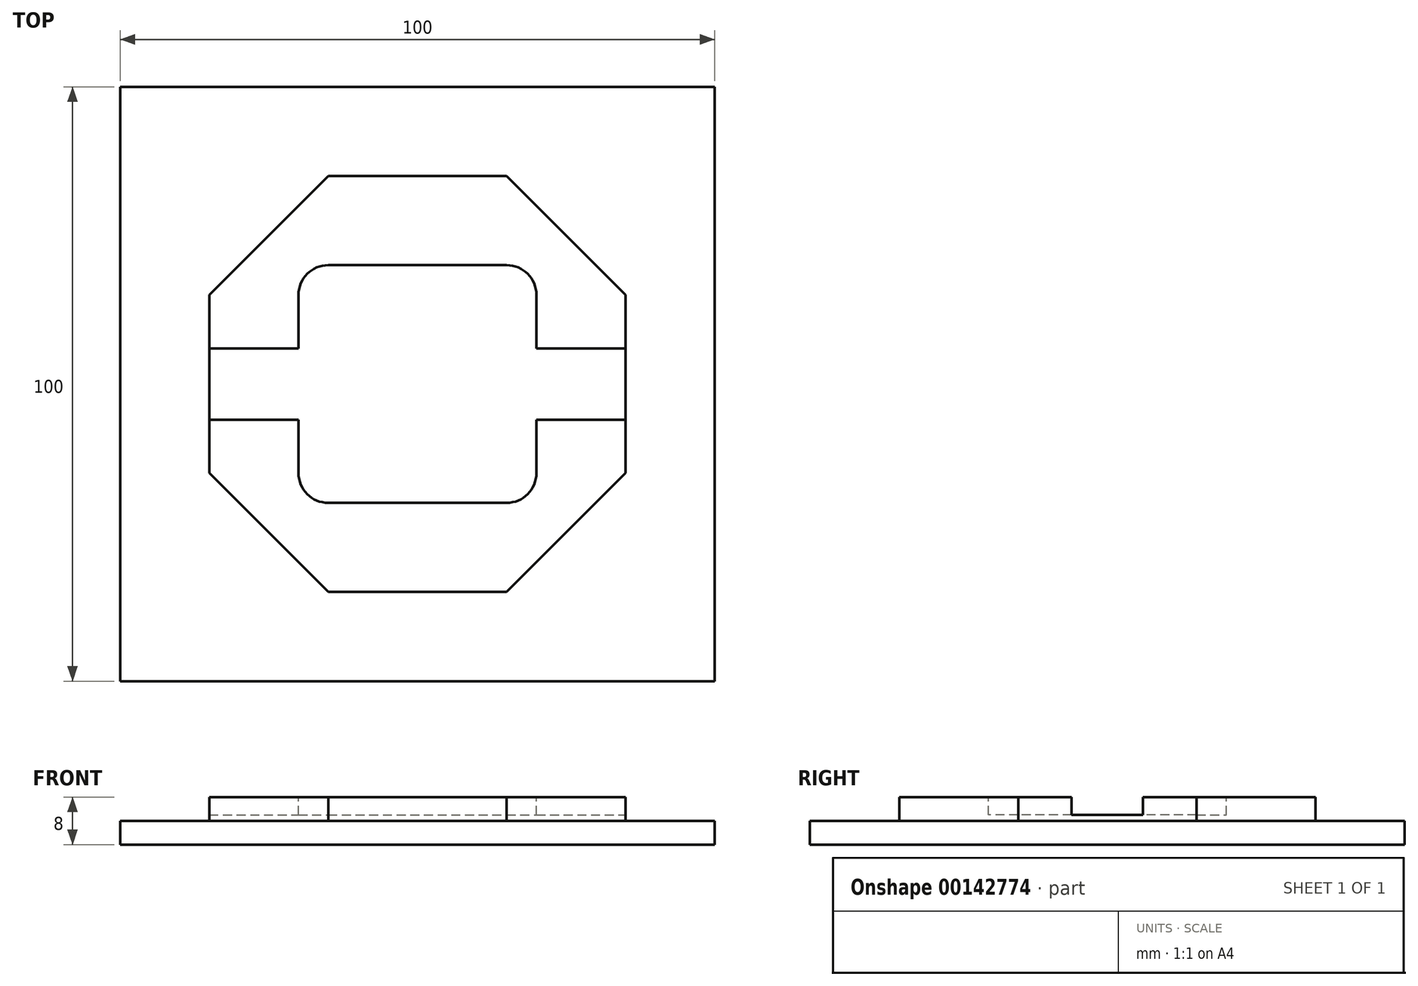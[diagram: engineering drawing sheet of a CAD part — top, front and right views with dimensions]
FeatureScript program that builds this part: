
annotation { "Feature Type Name" : "Feature", "Feature Type Description" : "" }
export const myFeature = defineFeature(function(context is Context, id is Id, definition is map)
    precondition{}
    {
        {
            var Q0;
            Q0=qCreatedBy(makeId("Top.planeOp"),FACE);
            var sketch = newSketch(context, id + "F0", { "sketchPlane" : qUnion([Q0])});
            skLineSegment(sketch, "E0.bottom", {"start": v(-50, -50) * mm, "end": v(50, -50) * mm});
            skLineSegment(sketch, "E0.top", {"start": v(-50, 50) * mm, "end": v(50, 50) * mm});
            skLineSegment(sketch, "E0.left", {"start": v(-50, -50) * mm, "end": v(-50, 50) * mm});
            skLineSegment(sketch, "E0.right", {"start": v(50, -50) * mm, "end": v(50, 50) * mm});
            skLineSegment(sketch, "E1", {"start": v(-50, 50) * mm, "end": v(50, -50) * mm, "construction": true});
            skSolve(sketch);
        }
        {
            var Q0;
            Q0=makeQuery(id+"F0.imprint","IMPRINT",FACE,{"disambiguationData":[TD([[makeQuery(id+"F0.imprint","IMPRINT",EDGE,{"derivedFrom":sQuery(id+"F0.wireOp",EDGE,"E0.bottom")}),1.0]])]});
            extrude(context, id + "F1", {"entities" : qUnion([Q0]), "depth" : 4 * mm});
        }
        {
            var Q0;
            Q0=makeQuery(id+"F1.opExtrude","CAP_FACE",FACE,{"disambiguationData":[OSD([sQuery(id+"F0.wireOp",EDGE,"E0.bottom"),sQuery(id+"F0.wireOp",EDGE,"E0.top"),sQuery(id+"F0.wireOp",EDGE,"E0.left"),sQuery(id+"F0.wireOp",EDGE,"E0.right")])],"isStart":false});
            var sketch = newSketch(context, id + "F2", { "sketchPlane" : qUnion([Q0])});
            skPoint(sketch, "E2.0", {"position": v(0, 0) * mm});
            skLineSegment(sketch, "E3.0", {"start": v(35, 15) * mm, "end": v(35, -15) * mm});
            skLineSegment(sketch, "E3.1", {"start": v(35, -15) * mm, "end": v(15, -35) * mm});
            skLineSegment(sketch, "E3.2", {"start": v(15, -35) * mm, "end": v(0, -35) * mm});
            skLineSegment(sketch, "E3.6", {"start": v(0, 35) * mm, "end": v(15, 35) * mm});
            skLineSegment(sketch, "E3.7", {"start": v(15, 35) * mm, "end": v(35, 15) * mm});
            skPoint(sketch, "E3.0.midPoint", {"position": v(35, 0) * mm});
            skLineSegment(sketch, "E4", {"start": v(0, -35) * mm, "end": v(0, 35) * mm, "construction": true});
            skLineSegment(sketch, "E5.MirrorCS", {"start": v(0, 35) * mm, "end": v(-15, 35) * mm});
            skLineSegment(sketch, "E6.MirrorCS", {"start": v(-15, 35) * mm, "end": v(-35, 15) * mm});
            skLineSegment(sketch, "E7.MirrorCS", {"start": v(-35, 15) * mm, "end": v(-35, -15) * mm});
            skLineSegment(sketch, "E8.MirrorCS", {"start": v(-35, -15) * mm, "end": v(-15, -35) * mm});
            skLineSegment(sketch, "E9.MirrorCS", {"start": v(-15, -35) * mm, "end": v(0, -35) * mm});
            skSolve(sketch);
        }
        {
            var Q0;
            Q0 = qSketchRegion(id + "F2", true);
            extrude(context, id + "F3", {"entities" : qUnion([Q0]), "operationType" : NewBodyOperationType.ADD, "depth" : 4 * mm});
        }
        {
            var Q0;
            Q0=makeQuery(id+"F3.opExtrude","CAP_FACE",FACE,{"disambiguationData":[OSD([sQuery(id+"F2.wireOp",EDGE,"E3.0"),sQuery(id+"F2.wireOp",EDGE,"E3.1"),sQuery(id+"F2.wireOp",EDGE,"E3.2"),sQuery(id+"F2.wireOp",EDGE,"E3.6"),sQuery(id+"F2.wireOp",EDGE,"E3.7"),sQuery(id+"F2.wireOp",EDGE,"E5.MirrorCS"),sQuery(id+"F2.wireOp",EDGE,"E6.MirrorCS"),sQuery(id+"F2.wireOp",EDGE,"E7.MirrorCS"),sQuery(id+"F2.wireOp",EDGE,"E8.MirrorCS"),sQuery(id+"F2.wireOp",EDGE,"E9.MirrorCS")])],"isStart":false});
            var sketch = newSketch(context, id + "F4", { "sketchPlane" : qUnion([Q0])});
            skLineSegment(sketch, "E10.bottom", {"start": v(-15, 20) * mm, "end": v(15, 20) * mm});
            skLineSegment(sketch, "E10.top", {"start": v(-15, -20) * mm, "end": v(15, -20) * mm});
            skLineSegment(sketch, "E10.left", {"start": v(-20, 15) * mm, "end": v(-20, 6) * mm});
            skLineSegment(sketch, "E10.right", {"start": v(20, 15) * mm, "end": v(20, 6) * mm});
            skLineSegment(sketch, "E11", {"start": v(-20, 20) * mm, "end": v(20, -20) * mm, "construction": true});
            skPoint(sketch, "E12.visualSharp", {"position": v(-20, 20) * mm});
            skArc(sketch, "E12.filletArc", {"start": v(-15, 20) * mm, "mid": v(-18.54, 18.54) * mm, "end": v(-20, 15) * mm});
            skPoint(sketch, "E13.visualSharp", {"position": v(20, 20) * mm});
            skArc(sketch, "E13.filletArc", {"start": v(20, 15) * mm, "mid": v(18.54, 18.54) * mm, "end": v(15, 20) * mm});
            skPoint(sketch, "E14.visualSharp", {"position": v(20, -20) * mm});
            skArc(sketch, "E14.filletArc", {"start": v(15, -20) * mm, "mid": v(18.54, -18.54) * mm, "end": v(20, -15) * mm});
            skPoint(sketch, "E15.visualSharp", {"position": v(-20, -20) * mm});
            skArc(sketch, "E15.filletArc", {"start": v(-20, -15) * mm, "mid": v(-18.54, -18.54) * mm, "end": v(-15, -20) * mm});
            skLineSegment(sketch, "E16.bottom", {"start": v(-35, 6) * mm, "end": v(-20, 6) * mm});
            skLineSegment(sketch, "E16.top", {"start": v(-35, -6) * mm, "end": v(-20, -6) * mm});
            skLineSegment(sketch, "E16.left", {"start": v(-35, 6) * mm, "end": v(-35, -6) * mm});
            skLineSegment(sketch, "E16.right", {"start": v(35, 6) * mm, "end": v(35, -6) * mm});
            skLineSegment(sketch, "E17.0", {"start": v(-35, 15) * mm, "end": v(-35, -15) * mm, "construction": true});
            skLineSegment(sketch, "E18.0", {"start": v(35, 15) * mm, "end": v(35, -15) * mm, "construction": true});
            skLineSegment(sketch, "E19", {"start": v(-35, -15) * mm, "end": v(35, -15) * mm, "construction": true});
            skLineSegment(sketch, "E20", {"start": v(35, -6) * mm, "end": v(-35, 6) * mm, "construction": true});
            skLineSegment(sketch, "E21.trimOffspring", {"start": v(-20, -6) * mm, "end": v(-20, -15) * mm});
            skLineSegment(sketch, "E22.trimOffspring", {"start": v(20, 6) * mm, "end": v(35, 6) * mm});
            skLineSegment(sketch, "E23.trimOffspring", {"start": v(20, -6) * mm, "end": v(35, -6) * mm});
            skLineSegment(sketch, "E24.trimOffspring", {"start": v(20, -6) * mm, "end": v(20, -15) * mm});
            skSolve(sketch);
        }
        {
            var Q0;
            Q0 = qSketchRegion(id + "F4", true);
            extrude(context, id + "F5", {"entities" : qUnion([Q0]), "operationType" : NewBodyOperationType.REMOVE, "oppositeDirection" : true, "depth" : 3 * mm});
        }
    });
